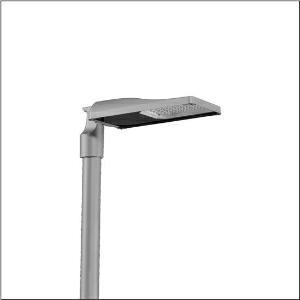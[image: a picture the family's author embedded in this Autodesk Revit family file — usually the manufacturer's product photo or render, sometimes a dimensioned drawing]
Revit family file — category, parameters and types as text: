
# Revit family: streetlight_sl_31_mini___stw1_0a_5xh2e7aa08ja_756d
name_source: partatom
category: Lighting Fixtures
units: mm (PartAtom-declared; Revit-internal decimal feet)

## family parameters
Cut with Voids When Loaded = No
Host = Face
Light Source = No
Part Type = Normal
Room Calculation Point = No
Round Connector Dimension = Use Diameter
Shared = No

## types (1)
- --- (1 x LED, 10010 lm, 81.1 W, 2200K)
    Apparent Load = 81 VA
    CIE Flux Codes = 39 75 98 100 100
    Color Rendering = 70
    Color Temperature = 2200K
    Default Elevation = 1800 mm
    Description = Streetlight SL 31 mini, mast luminaire, primary light control with lens, of PMMA, primary optical cover: cover, of toughened safety glass, transparent, light distribution: STW1.0a, light emission: direct distribution, primary light characteristic: asymmetric, installation type: post-top, side-entry, LED, High Power LED, rated luminous flux: 10.010lm, luminous efficacy: 123lm/W, light colour: 722, colour temperature: 2200K, control: overheat protection, intelligent temperature release in ECG and LED module, constant luminous flux control, time-dependent luminous flux control, flexible luminous flux parameterisation, presetting dimming linear, with cable H07RN-F 2x 1.5mm², mains connection: 220..240V, AC, 50/60Hz, connection cable pre-assembled, cable length: 10,5m, start of lifetime: 81W, end of service life: 88W, reduction: 36W, luminaire housing, of diecast aluminium, powder-coated, Siteco® metallic grey (DB 702S), corrosivity category C5 high according to DIN EN ISO 12944, no sealing on luminaire upper side, inclination: -15°..+20° (post-top) | -20°..+20° (side-entry), adjustable in 5° steps, mast flange (76/60mm) included as standard, multi-level sealing system, sealing non-destructively replaceable, protection rating (complete): IP66, insulation class (complete): insulation class II (safety insulation), certification: CE, ENEC, ENEC+, VDE, UKCA, impact resistance: IK09, permissible operating ambient temperature for outdoor applications: -40..+50°C, standard-compliant lighting for roads and squares, packaging unit: 1 piece

Light Distribution: STW1.0a
    Height = 76 mm
    Lamp = 1 x LED
    Lamp Light Flux = 10010 lm
    Lamp Power = 81.1 W
    Lamp count = 1
    Length = 547 mm
    Luminous efficacy = 123 lm/W
    Manufacturer = Siteco
    ModVariant = No
    Model = 5XH2E7AA08JA
    Number of Poles = 1
    OnlyDefault = Yes
    Power Factor = 1
    Product Name = Streetlight SL 31 mini | STW1.0a
    Product group = mast luminaire | pylon top
    ProductGroupID = 6100
    Protection Class = Protection class II
    Protection Degree = IP 66
    RLX_Detail_Level = 1
    RLX_Emergency_Light_Flux = 0 lm
    RLX_Emergency_Type = 0
    RLX_Emergency_Type_DB = No
    RlxData = <blob elided: 39997 chars, md5=5b5e645e>
    Socket = socket
    Standby Power = 0 W
    System Light Flux = 10010 lm
    System Power = 81 W
    Type Comments = factory setting: luminous flux: 100 % | dim-lin: 254 | 860 mA
    Type Image = l_1300326.jpg
    URL = http://relux.com
    VarID = @adj_007495
    Voltage = 0 V
    Weight = 0.00 kg
    Width = 265 mm

## geometry (parser evidence)
native form markers: Blend x4, Sweep x12
no freeform markers — native parametric forms only
